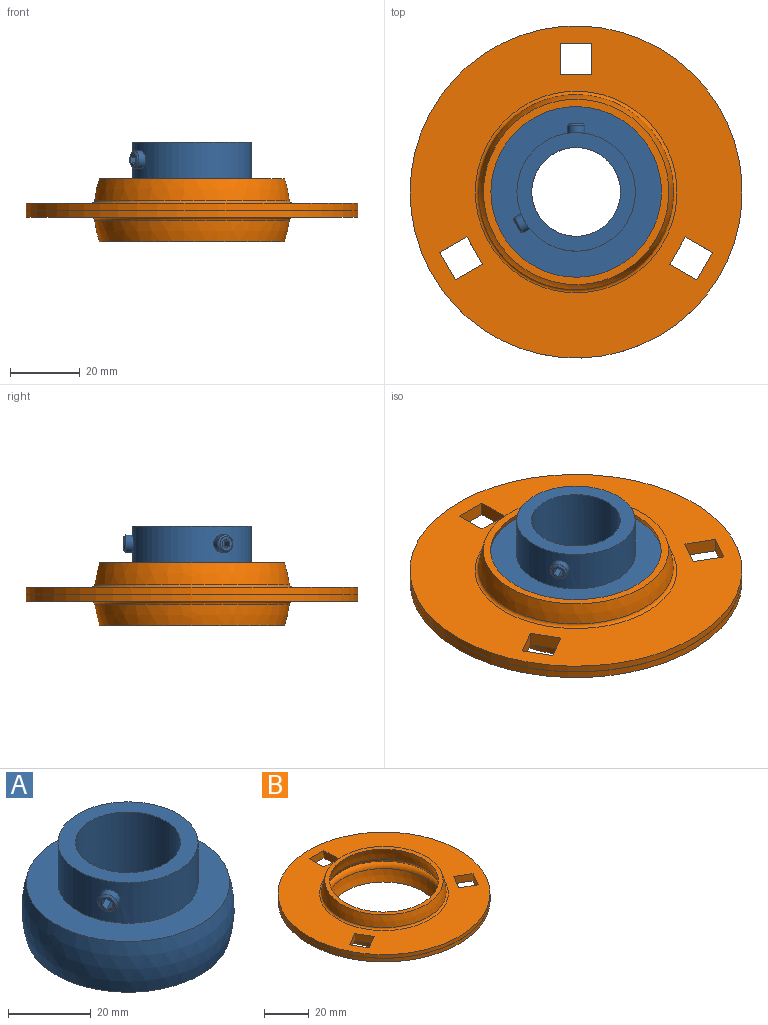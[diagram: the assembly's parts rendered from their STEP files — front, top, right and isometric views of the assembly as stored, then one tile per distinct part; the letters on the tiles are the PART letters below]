
ASSEMBLY  parts=2 mates=1
PART A: 26 faces, bbox 51.5x51.5x27 mm
  f0: plane 4.02x4.02mm, normal (0,1,0), area 7.3mm2, adj f6,f11,f12,f13,f14,f15,f16
  f1: cylinder r=16.95mm len=33.9mm, axis (0,0,-1), area 1238.6mm2, adj f2,f5,f7,f10
  f2: plane 33.9x33.9mm, normal (0,0,1), area 395.9mm2, adj f1,f25
  f3: plane 49.25x49.25mm, normal (0,0,-1), area 1398mm2, adj f4,f25
  f4: sphere r=25.74mm, area 2425.9mm2, adj f3,f5
  f5: plane 49.25x49.25mm, normal (0,0,1), area 1002.2mm2, adj f1,f4
  f6: cone r=2.01mm half-angle=45deg, axis (0,-1,0), area 9.8mm2, adj f0,f7
  f7: cylinder r=2.5mm len=5mm, axis (0,-1,0), area 33.8mm2, adj f1,f6
  f8: plane 4.02x3.48mm, normal (-0.87,-0.5,0), area 7.3mm2, adj f9,f18,f19,f20,f21,f22,f23
  f9: cone r=2.01mm half-angle=45deg, axis (0.87,0.5,0), area 9.8mm2, adj f8,f10
  f10: cylinder r=2.5mm len=5.45mm, axis (0.87,0.5,0), area 33.8mm2, adj f1,f9
  f11: plane 3.3x1.44mm, normal (1,0,0), area 4.8mm2, adj f0,f12,f16,f17
  f12: plane 3.3x1.25mm, normal (0.5,0,0.87), area 4.8mm2, adj f0,f11,f13,f17
  f13: plane 3.3x1.25mm, normal (-0.5,0,0.87), area 4.8mm2, adj f0,f12,f14,f17
  f14: plane 3.3x1.44mm, normal (-1,0,0), area 4.8mm2, adj f0,f13,f15,f17
  f15: plane 3.3x1.25mm, normal (-0.5,0,-0.87), area 4.8mm2, adj f0,f14,f16,f17
  f16: plane 3.3x1.25mm, normal (0.5,0,-0.87), area 4.8mm2, adj f0,f11,f15,f17
  f17: plane 2.89x2.5mm, normal (0,1,0), area 5.4mm2, adj f11,f12,f13,f14,f15,f16
  f18: plane 2.86x1.65mm, normal (0.5,-0.87,0), area 4.8mm2, adj f8,f19,f23,f24
  f19: plane 3.48x2.73mm, normal (0.25,-0.43,0.87), area 4.8mm2, adj f8,f18,f20,f24
  f20: plane 3.48x2.73mm, normal (-0.25,0.43,0.87), area 4.8mm2, adj f8,f19,f21,f24
  f21: plane 2.86x1.65mm, normal (-0.5,0.87,0), area 4.8mm2, adj f8,f20,f22,f24
  f22: plane 3.48x2.73mm, normal (-0.25,0.43,-0.87), area 4.8mm2, adj f8,f21,f23,f24
  f23: plane 3.48x2.73mm, normal (0.25,-0.43,-0.87), area 4.8mm2, adj f8,f18,f22,f24
  f24: plane 2.89x2.17mm, normal (-0.87,-0.5,0), area 5.4mm2, adj f18,f19,f20,f21,f22,f23
  f25: cylinder r=12.7mm len=27mm, axis (0,0,1), area 2154.5mm2, adj f2,f3
PART B: 28 faces, bbox 95x95x18 mm
  f0: plane 95x95mm, normal (0,0,-1), area 4231.4mm2, adj f7,f8,f16,f17,f18,f19,f20,f21
  f1: plane 95x95mm, normal (0,0,1), area 4231.4mm2, adj f14,f15,f16,f17,f18,f19,f20,f21
  f2: cone r=47.5mm half-angle=45deg, axis (0,0,-1), area 8.4mm2, adj f8,f13
  f3: torus R=28.84mm, axis (0,0,-1), area 747mm2, adj f4,f12
  f4: sphere r=26mm, area 1030.9mm2, adj f3,f5
  f5: plane 53.03x53.03mm, normal (0,0,-1), area 339.3mm2, adj f4,f6
  f6: sphere r=28mm, area 1073.8mm2, adj f5,f7
  f7: torus R=28.84mm, axis (0,0,-1), area 260.3mm2, adj f0,f6
  f8: cylinder r=47.5mm len=95mm, axis (0,0,-1), area 590.9mm2, adj f0,f2
  f9: sphere r=28mm, area 1073.8mm2, adj f10,f15
  f10: plane 53.03x53.03mm, normal (0,0,1), area 339.3mm2, adj f9,f11
  f11: sphere r=26mm, area 1030.9mm2, adj f10,f12
  f12: torus R=28.84mm, axis (0,0,-1), area 747mm2, adj f3,f11
  f13: cone r=47.48mm half-angle=45deg, axis (0,0,1), area 8.4mm2, adj f2,f14
  f14: cylinder r=47.5mm len=95mm, axis (0,0,-1), area 590.9mm2, adj f1,f13
  f15: torus R=28.84mm, axis (0,0,-1), area 260.3mm2, adj f1,f9
  f16: plane 9x4mm, normal (0,-1,0), area 36mm2, adj f0,f1,f17,f19
  f17: plane 9x4mm, normal (1,0,0), area 36mm2, adj f0,f1,f16,f18
  f18: plane 9x4mm, normal (0,1,0), area 36mm2, adj f0,f1,f17,f19
  f19: plane 9x4mm, normal (-1,0,0), area 36mm2, adj f0,f1,f16,f18
  f20: plane 7.79x4.5mm, normal (0.87,-0.5,0), area 36mm2, adj f0,f1,f21,f23
  f21: plane 7.79x4.5mm, normal (0.5,0.87,0), area 36mm2, adj f0,f1,f20,f22
  f22: plane 7.79x4.5mm, normal (-0.87,0.5,0), area 36mm2, adj f0,f1,f21,f23
  f23: plane 7.79x4.5mm, normal (-0.5,-0.87,0), area 36mm2, adj f0,f1,f20,f22
  f24: plane 7.79x4.5mm, normal (0.5,-0.87,0), area 36mm2, adj f0,f1,f25,f27
  f25: plane 7.79x4.5mm, normal (0.87,0.5,0), area 36mm2, adj f0,f1,f24,f26
  f26: plane 7.79x4.5mm, normal (-0.5,0.87,0), area 36mm2, adj f0,f1,f25,f27
  f27: plane 7.79x4.5mm, normal (-0.87,-0.5,0), area 36mm2, adj f0,f1,f24,f26
PLACE A t=(0,0,0.02)mm
PLACE B at identity fixed
MATE ball A.f25 <-> B.f2  axis (0,0,1) through (0,0,0.02)mm
